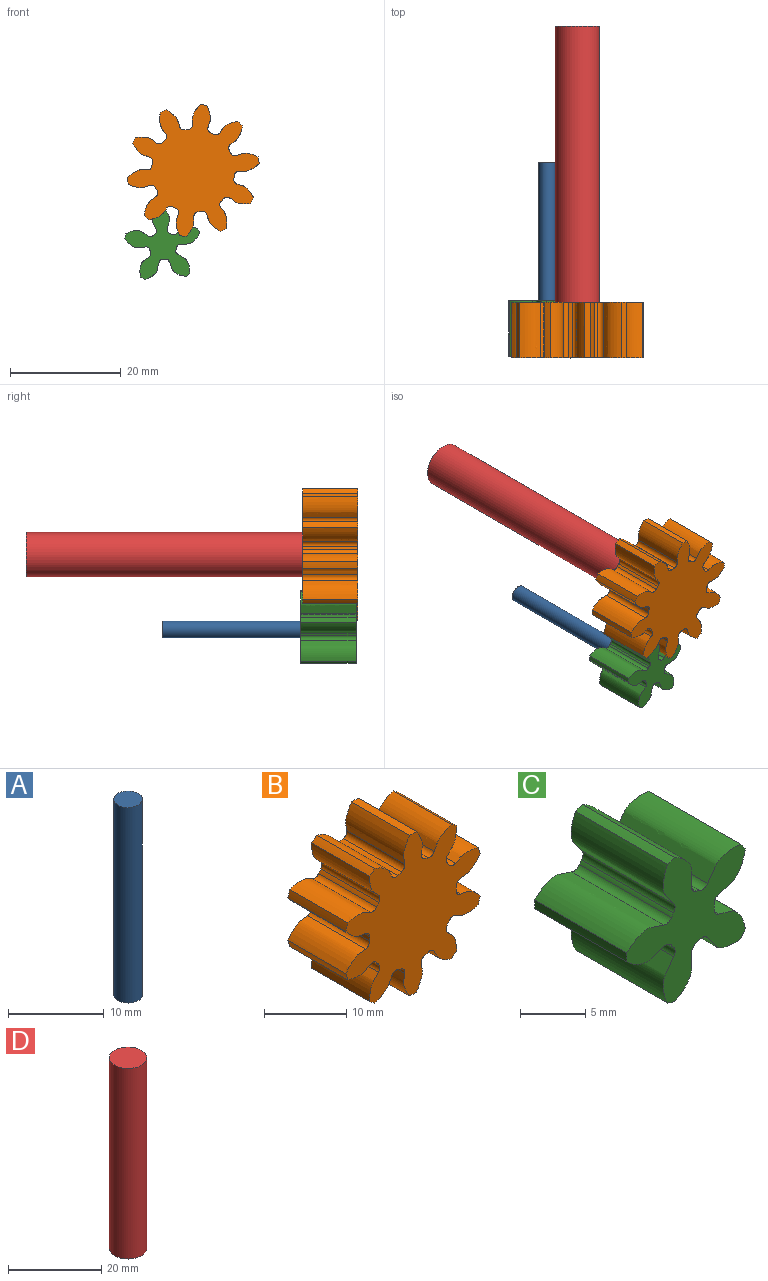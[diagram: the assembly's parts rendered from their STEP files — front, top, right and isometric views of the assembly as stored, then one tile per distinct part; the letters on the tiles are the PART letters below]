
ASSEMBLY  parts=4 mates=2
PART A: 3 faces, bbox 3x3x25 mm
  f0: cylinder r=1.5mm len=25mm, axis (0,0,-1), area 235.6mm2, adj f1,f2
  f1: plane 3x3mm, normal (0,0,1), area 7.1mm2, adj f0
  f2: plane 3x3mm, normal (0,0,-1), area 7.1mm2, adj f0
PART B: 62 faces, bbox 23.2x10x24 mm
  f0: cylinder r=12mm len=10mm, axis (0,1,0), area 11.7mm2, adj f9,f11,f52,f59
  f1: cylinder r=12mm len=10mm, axis (0,1,0), area 11.7mm2, adj f9,f11,f12,f54
  f2: cylinder r=12mm len=10mm, axis (0,1,0), area 11.7mm2, adj f9,f11,f42,f49
  f3: cylinder r=12mm len=10mm, axis (0,1,0), area 11.7mm2, adj f9,f11,f44,f57
  f4: cylinder r=12mm len=10mm, axis (0,1,0), area 11.7mm2, adj f9,f11,f32,f39
  f5: cylinder r=12mm len=10mm, axis (0,1,0), area 11.7mm2, adj f9,f11,f27,f34
  f6: cylinder r=12mm len=10mm, axis (0,1,0), area 11.7mm2, adj f9,f11,f22,f29
  f7: cylinder r=12mm len=10mm, axis (0,1,0), area 11.7mm2, adj f9,f11,f24,f47
  f8: cylinder r=12mm len=10mm, axis (0,1,0), area 11.7mm2, adj f9,f11,f19,f37
  f9: plane 24.04x23.21mm, normal (0,-1,0), area 300.5mm2, adj f0,f1,f2,f3,f4,f5,f6,f7
  f10: cylinder r=12mm len=10mm, axis (0,1,0), area 11.7mm2, adj f9,f11,f14,f17
  f11: plane 24.04x23.21mm, normal (0,1,0), area 300.5mm2, adj f0,f1,f2,f3,f4,f5,f6,f7
  f12: extruded ~10x3.38mm, area 40.6mm2, adj f1,f9,f11,f15
  f13: cylinder r=7.5mm len=10mm, axis (0,1,0), area 6.4mm2, adj f9,f11,f15,f16
  f14: extruded ~10x3.38mm, area 40.6mm2, adj f9,f10,f11,f16
  f15: cylinder r=0.82mm len=10mm, axis (0,1,0), area 12.1mm2, adj f9,f11,f12,f13
  f16: cylinder r=0.82mm len=10mm, axis (0,1,0), area 12.1mm2, adj f9,f11,f13,f14
  f17: extruded ~10x3.89mm, area 40.6mm2, adj f9,f10,f11,f20
  f18: cylinder r=7.5mm len=10mm, axis (0,1,0), area 6.4mm2, adj f9,f11,f20,f21
  f19: extruded ~10x3.58mm, area 40.6mm2, adj f8,f9,f11,f21
  f20: cylinder r=0.82mm len=10mm, axis (0,1,0), area 12.1mm2, adj f9,f11,f17,f18
  f21: cylinder r=0.82mm len=10mm, axis (0,1,0), area 12.1mm2, adj f9,f11,f18,f19
  f22: extruded ~10x3.38mm, area 40.6mm2, adj f6,f9,f11,f25
  f23: cylinder r=7.5mm len=10mm, axis (0,1,0), area 6.4mm2, adj f9,f11,f25,f26
  f24: extruded ~10x3.38mm, area 40.6mm2, adj f7,f9,f11,f26
  f25: cylinder r=0.82mm len=10mm, axis (0,1,0), area 12.1mm2, adj f9,f11,f22,f23
  f26: cylinder r=0.82mm len=10mm, axis (0,1,0), area 12.1mm2, adj f9,f11,f23,f24
  f27: extruded ~10x3.58mm, area 40.6mm2, adj f5,f9,f11,f30
  f28: cylinder r=7.5mm len=10mm, axis (0,1,0), area 6.4mm2, adj f9,f11,f30,f31
  f29: extruded ~10x3.89mm, area 40.6mm2, adj f6,f9,f11,f31
  f30: cylinder r=0.82mm len=10mm, axis (0,1,0), area 12.1mm2, adj f9,f11,f27,f28
  f31: cylinder r=0.82mm len=10mm, axis (0,1,0), area 12.1mm2, adj f9,f11,f28,f29
  f32: extruded ~10x3.82mm, area 40.6mm2, adj f4,f9,f11,f35
  f33: cylinder r=7.5mm len=10mm, axis (0,1,0), area 6.4mm2, adj f9,f11,f35,f36
  f34: extruded ~10x2.92mm, area 40.6mm2, adj f5,f9,f11,f36
  f35: cylinder r=0.82mm len=10mm, axis (0,1,0), area 12.1mm2, adj f9,f11,f32,f33
  f36: cylinder r=0.82mm len=10mm, axis (0,1,0), area 12.1mm2, adj f9,f11,f33,f34
  f37: extruded ~10x2.92mm, area 40.6mm2, adj f8,f9,f11,f40
  f38: cylinder r=7.5mm len=10mm, axis (0,1,0), area 6.4mm2, adj f9,f11,f40,f41
  f39: extruded ~10x3.82mm, area 40.6mm2, adj f4,f9,f11,f41
  f40: cylinder r=0.82mm len=10mm, axis (0,1,0), area 12.1mm2, adj f9,f11,f37,f38
  f41: cylinder r=0.82mm len=10mm, axis (0,1,0), area 12.1mm2, adj f9,f11,f38,f39
  f42: extruded ~10x2.92mm, area 40.6mm2, adj f2,f9,f11,f45
  f43: cylinder r=7.5mm len=10mm, axis (0,1,0), area 6.4mm2, adj f9,f11,f45,f46
  f44: extruded ~10x3.82mm, area 40.6mm2, adj f3,f9,f11,f46
  f45: cylinder r=0.82mm len=10mm, axis (0,1,0), area 12.1mm2, adj f9,f11,f42,f43
  f46: cylinder r=0.82mm len=10mm, axis (0,1,0), area 12.1mm2, adj f9,f11,f43,f44
  f47: extruded ~10x3.89mm, area 40.6mm2, adj f7,f9,f11,f50
  f48: cylinder r=7.5mm len=10mm, axis (0,1,0), area 6.4mm2, adj f9,f11,f50,f51
  f49: extruded ~10x3.58mm, area 40.6mm2, adj f2,f9,f11,f51
  f50: cylinder r=0.82mm len=10mm, axis (0,1,0), area 12.1mm2, adj f9,f11,f47,f48
  f51: cylinder r=0.82mm len=10mm, axis (0,1,0), area 12.1mm2, adj f9,f11,f48,f49
  f52: extruded ~10x3.58mm, area 40.6mm2, adj f0,f9,f11,f55
  f53: cylinder r=7.5mm len=10mm, axis (0,1,0), area 6.4mm2, adj f9,f11,f55,f56
  f54: extruded ~10x3.89mm, area 40.6mm2, adj f1,f9,f11,f56
  f55: cylinder r=0.82mm len=10mm, axis (0,1,0), area 12.1mm2, adj f9,f11,f52,f53
  f56: cylinder r=0.82mm len=10mm, axis (0,1,0), area 12.1mm2, adj f9,f11,f53,f54
  f57: extruded ~10x3.82mm, area 40.6mm2, adj f3,f9,f11,f60
  f58: cylinder r=7.5mm len=10mm, axis (0,1,0), area 6.4mm2, adj f9,f11,f60,f61
  f59: extruded ~10x2.92mm, area 40.6mm2, adj f0,f9,f11,f61
  f60: cylinder r=0.82mm len=10mm, axis (0,1,0), area 12.1mm2, adj f9,f11,f57,f58
  f61: cylinder r=0.82mm len=10mm, axis (0,1,0), area 12.1mm2, adj f9,f11,f58,f59
PART C: 32 faces, bbox 13x10x13.7 mm
  f0: cylinder r=7mm len=10mm, axis (0,1,0), area 8.3mm2, adj f4,f6,f12,f29
  f1: cylinder r=7mm len=10mm, axis (0,1,0), area 8.3mm2, adj f4,f6,f24,f27
  f2: cylinder r=7mm len=10mm, axis (0,1,0), area 8.3mm2, adj f4,f6,f7,f19
  f3: cylinder r=7mm len=10mm, axis (0,1,0), area 8.3mm2, adj f4,f6,f14,f17
  f4: plane 13.68x12.99mm, normal (0,-1,0), area 74.3mm2, adj f0,f1,f2,f3,f5,f7,f8,f9
  f5: cylinder r=7mm len=10mm, axis (0,1,0), area 8.3mm2, adj f4,f6,f9,f22
  f6: plane 13.68x12.99mm, normal (0,1,0), area 74.3mm2, adj f0,f1,f2,f3,f5,f7,f8,f9
  f7: extruded ~10x2.92mm, area 44.2mm2, adj f2,f4,f6,f10
  f8: cylinder r=2.5mm len=10mm, axis (0,1,0), area 4mm2, adj f4,f6,f10,f11
  f9: extruded ~10x2.92mm, area 44.2mm2, adj f4,f5,f6,f11
  f10: cylinder r=0.7mm len=10mm, axis (0,1,0), area 9.4mm2, adj f4,f6,f7,f8
  f11: cylinder r=0.7mm len=10mm, axis (0,1,0), area 9.4mm2, adj f4,f6,f8,f9
  f12: extruded ~10x4.04mm, area 44.2mm2, adj f0,f4,f6,f15
  f13: cylinder r=2.5mm len=10mm, axis (0,1,0), area 4mm2, adj f4,f6,f15,f16
  f14: extruded ~10x4.02mm, area 44.2mm2, adj f3,f4,f6,f16
  f15: cylinder r=0.7mm len=10mm, axis (0,1,0), area 9.4mm2, adj f4,f6,f12,f13
  f16: cylinder r=0.7mm len=10mm, axis (0,1,0), area 9.4mm2, adj f4,f6,f13,f14
  f17: extruded ~10x3.66mm, area 44.2mm2, adj f3,f4,f6,f20
  f18: cylinder r=2.5mm len=10mm, axis (0,1,0), area 4mm2, adj f4,f6,f20,f21
  f19: extruded ~10x3.61mm, area 44.2mm2, adj f2,f4,f6,f21
  f20: cylinder r=0.7mm len=10mm, axis (0,1,0), area 9.4mm2, adj f4,f6,f17,f18
  f21: cylinder r=0.7mm len=10mm, axis (0,1,0), area 9.4mm2, adj f4,f6,f18,f19
  f22: extruded ~10x3.61mm, area 44.2mm2, adj f4,f5,f6,f25
  f23: cylinder r=2.5mm len=10mm, axis (0,1,0), area 4mm2, adj f4,f6,f25,f26
  f24: extruded ~10x3.66mm, area 44.2mm2, adj f1,f4,f6,f26
  f25: cylinder r=0.7mm len=10mm, axis (0,1,0), area 9.4mm2, adj f4,f6,f22,f23
  f26: cylinder r=0.7mm len=10mm, axis (0,1,0), area 9.4mm2, adj f4,f6,f23,f24
  f27: extruded ~10x4.02mm, area 44.2mm2, adj f1,f4,f6,f30
  f28: cylinder r=2.5mm len=10mm, axis (0,1,0), area 4mm2, adj f4,f6,f30,f31
  f29: extruded ~10x4.04mm, area 44.2mm2, adj f0,f4,f6,f31
  f30: cylinder r=0.7mm len=10mm, axis (0,1,0), area 9.4mm2, adj f4,f6,f27,f28
  f31: cylinder r=0.7mm len=10mm, axis (0,1,0), area 9.4mm2, adj f4,f6,f28,f29
PART D: 3 faces, bbox 8x8x50 mm
  f0: cylinder r=4mm len=50mm, axis (0,0,-1), area 1256.6mm2, adj f1,f2
  f1: plane 8x8mm, normal (0,0,1), area 50.3mm2, adj f0
  f2: plane 8x8mm, normal (0,0,-1), area 50.3mm2, adj f0
PLACE A rot(axis=(-0.58,0.58,0.58),120deg) t=(32.2,58.96,-57.21)mm
PLACE B rot(axis=(0,1,0),45deg) t=(4.94,46.12,-2.4)mm
PLACE C rot(axis=(0,-1,0),130.2deg) t=(-0.55,46.46,-15.94)mm
PLACE D rot(axis=(0.55,0.59,-0.59),122.8deg) t=(-19.69,71.12,31.47)mm
MATE revolute B.f0 <-> D.f0  axis (0,1,0) through (4.94,46.12,-2.4)mm
MATE revolute A.f0 <-> C.f0  axis (0,-1,0) through (-0.55,46.46,-15.94)mm
